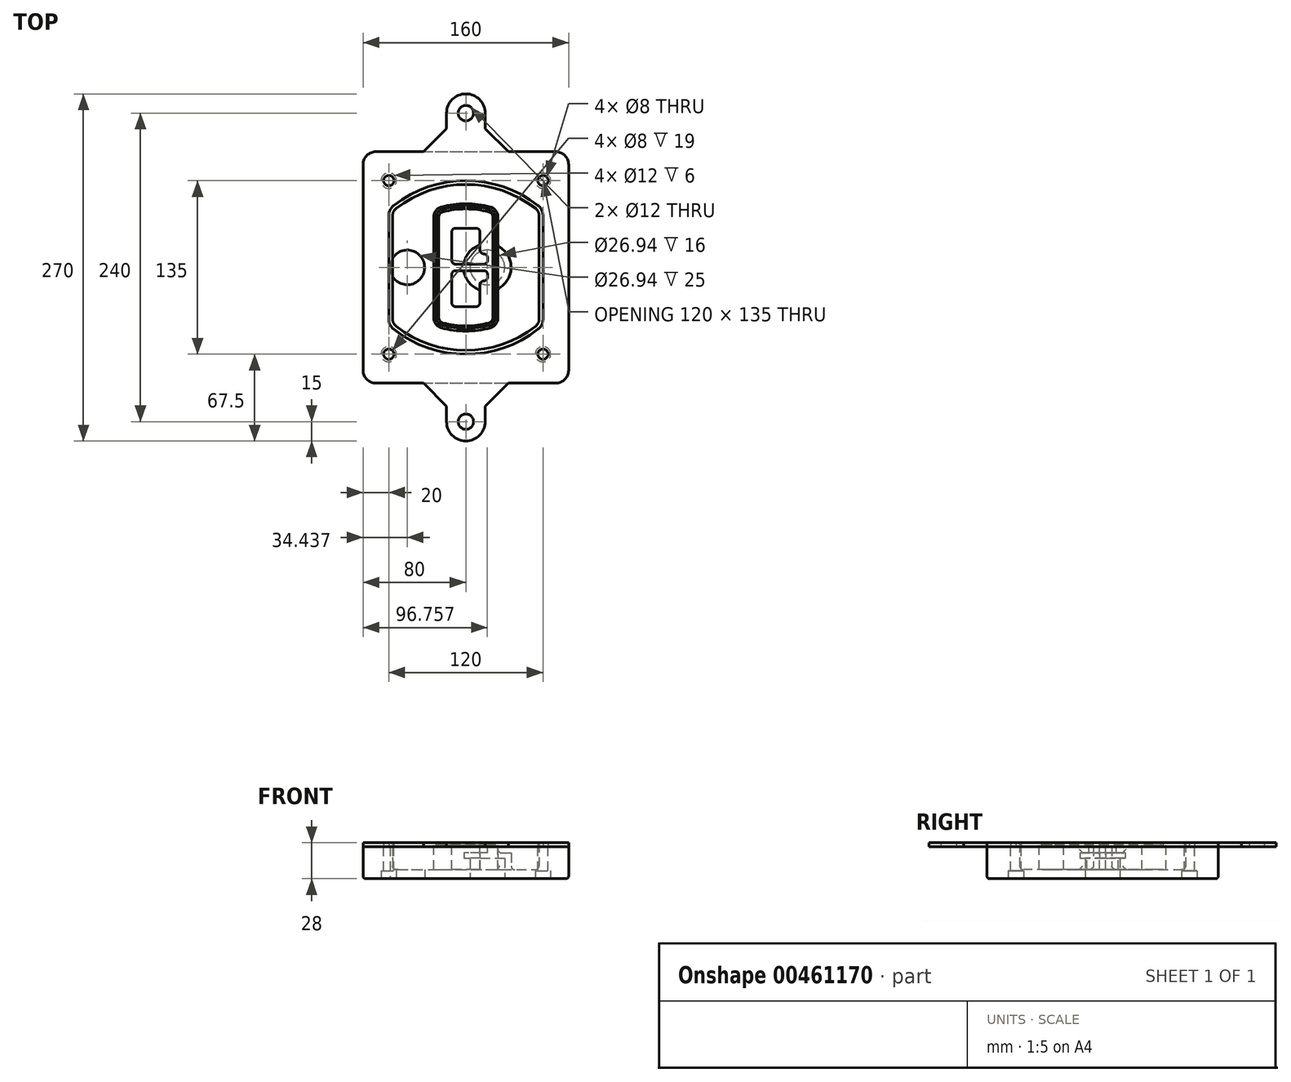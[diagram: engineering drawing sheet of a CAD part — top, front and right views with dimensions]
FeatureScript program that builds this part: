
annotation { "Feature Type Name" : "Feature", "Feature Type Description" : "" }
export const myFeature = defineFeature(function(context is Context, id is Id, definition is map)
    precondition{}
    {
        {
            var Q0;
            Q0=qCreatedBy(makeId("Top.planeOp"),FACE);
            var sketch = newSketch(context, id + "F0", { "sketchPlane" : qUnion([Q0])});
            skPoint(sketch, "E0.rect.middle", {"position": v(0, 0) * mm});
            skLineSegment(sketch, "E1.bottom", {"start": v(-70, -90) * mm, "end": v(70, -90) * mm});
            skLineSegment(sketch, "E1.top", {"start": v(-70, 90) * mm, "end": v(70, 90) * mm});
            skLineSegment(sketch, "E1.left", {"start": v(-80, -80) * mm, "end": v(-80, 80) * mm});
            skLineSegment(sketch, "E1.right", {"start": v(80, -80) * mm, "end": v(80, 80) * mm});
            skLineSegment(sketch, "E2", {"start": v(-80, 90) * mm, "end": v(80, -90) * mm, "construction": true});
            skLineSegment(sketch, "E3", {"start": v(80, 90) * mm, "end": v(-80, -90) * mm, "construction": true});
            skCircle(sketch, "E4", {"center": v(-60, 67.5) * mm, "radius": 4 * mm});
            skCircle(sketch, "E5", {"center": v(60, 67.5) * mm, "radius": 4 * mm});
            skCircle(sketch, "E6", {"center": v(60, -67.5) * mm, "radius": 4 * mm});
            skCircle(sketch, "E7", {"center": v(-60, -67.5) * mm, "radius": 4 * mm});
            skLineSegment(sketch, "E8", {"start": v(-60, 67.5) * mm, "end": v(60, 67.5) * mm, "construction": true});
            skLineSegment(sketch, "E9", {"start": v(60, 67.5) * mm, "end": v(60, -67.5) * mm, "construction": true});
            skLineSegment(sketch, "E10", {"start": v(60, -67.5) * mm, "end": v(-60, -67.5) * mm, "construction": true});
            skLineSegment(sketch, "E11", {"start": v(-60, -67.5) * mm, "end": v(-60, 67.5) * mm, "construction": true});
            skLineSegment(sketch, "E12", {"start": v(-60, 40.3) * mm, "end": v(-60, -40.3) * mm});
            skLineSegment(sketch, "E13", {"start": v(60, 40.3) * mm, "end": v(60, -40.3) * mm});
            skArc(sketch, "E14", {"start": v(56.15, 48.18) * mm, "mid": v(0, 67.5) * mm, "end": v(-56.15, 48.18) * mm});
            skArc(sketch, "E15", {"start": v(-56.15, -48.18) * mm, "mid": v(0, -67.5) * mm, "end": v(56.15, -48.18) * mm});
            skLineSegment(sketch, "E16", {"start": v(-60, 0) * mm, "end": v(60, 0) * mm, "construction": true});
            skPoint(sketch, "E17.visualSharp", {"position": v(-60, -45) * mm});
            skArc(sketch, "E17.filletArc", {"start": v(-60, -40.3) * mm, "mid": v(-58.99, -44.68) * mm, "end": v(-56.15, -48.18) * mm});
            skPoint(sketch, "E18.visualSharp", {"position": v(-60, 45) * mm});
            skArc(sketch, "E18.filletArc", {"start": v(-56.15, 48.18) * mm, "mid": v(-58.99, 44.68) * mm, "end": v(-60, 40.3) * mm});
            skPoint(sketch, "E19.visualSharp", {"position": v(60, 45) * mm});
            skArc(sketch, "E19.filletArc", {"start": v(60, 40.3) * mm, "mid": v(58.99, 44.68) * mm, "end": v(56.15, 48.18) * mm});
            skPoint(sketch, "E20.visualSharp", {"position": v(60, -45) * mm});
            skArc(sketch, "E20.filletArc", {"start": v(56.15, -48.18) * mm, "mid": v(58.99, -44.68) * mm, "end": v(60, -40.3) * mm});
            skPoint(sketch, "E21.visualSharp", {"position": v(-80, 90) * mm});
            skArc(sketch, "E21.filletArc", {"start": v(-70, 90) * mm, "mid": v(-77.07, 87.07) * mm, "end": v(-80, 80) * mm});
            skPoint(sketch, "E22.visualSharp", {"position": v(80, 90) * mm});
            skArc(sketch, "E22.filletArc", {"start": v(80, 80) * mm, "mid": v(77.07, 87.07) * mm, "end": v(70, 90) * mm});
            skPoint(sketch, "E23.visualSharp", {"position": v(80, -90) * mm});
            skArc(sketch, "E23.filletArc", {"start": v(70, -90) * mm, "mid": v(77.07, -87.07) * mm, "end": v(80, -80) * mm});
            skPoint(sketch, "E24.visualSharp", {"position": v(-80, -90) * mm});
            skArc(sketch, "E24.filletArc", {"start": v(-80, -80) * mm, "mid": v(-77.07, -87.07) * mm, "end": v(-70, -90) * mm});
            skArc(sketch, "E25.0", {"start": v(57, 40.3) * mm, "mid": v(56.3, 43.36) * mm, "end": v(54.3, 45.81) * mm});
            skLineSegment(sketch, "E25.1", {"start": v(57, 40.3) * mm, "end": v(57, -40.3) * mm});
            skArc(sketch, "E25.2", {"start": v(54.3, -45.81) * mm, "mid": v(56.3, -43.36) * mm, "end": v(57, -40.3) * mm});
            skArc(sketch, "E25.3", {"start": v(-54.3, -45.81) * mm, "mid": v(0, -64.5) * mm, "end": v(54.3, -45.81) * mm});
            skArc(sketch, "E25.4", {"start": v(-57, -40.3) * mm, "mid": v(-56.3, -43.36) * mm, "end": v(-54.3, -45.81) * mm});
            skArc(sketch, "E25.5", {"start": v(54.3, 45.81) * mm, "mid": v(0, 64.5) * mm, "end": v(-54.3, 45.81) * mm});
            skLineSegment(sketch, "E25.6", {"start": v(-57, 40.3) * mm, "end": v(-57, -40.3) * mm});
            skArc(sketch, "E25.7", {"start": v(-54.3, 45.81) * mm, "mid": v(-56.3, 43.36) * mm, "end": v(-57, 40.3) * mm});
            skArc(sketch, "E26.0", {"start": v(-58.62, 51.33) * mm, "mid": v(-62.58, 46.43) * mm, "end": v(-64, 40.3) * mm});
            skArc(sketch, "E26.1", {"start": v(58.62, 51.33) * mm, "mid": v(0, 71.5) * mm, "end": v(-58.62, 51.33) * mm});
            skArc(sketch, "E26.2", {"start": v(64, 40.3) * mm, "mid": v(62.58, 46.43) * mm, "end": v(58.62, 51.33) * mm});
            skLineSegment(sketch, "E26.3", {"start": v(64, 40.3) * mm, "end": v(64, -40.3) * mm});
            skArc(sketch, "E26.4", {"start": v(58.62, -51.33) * mm, "mid": v(62.58, -46.43) * mm, "end": v(64, -40.3) * mm});
            skLineSegment(sketch, "E26.5", {"start": v(-64, 40.3) * mm, "end": v(-64, -40.3) * mm});
            skArc(sketch, "E26.6", {"start": v(-58.62, -51.33) * mm, "mid": v(0, -71.5) * mm, "end": v(58.62, -51.33) * mm});
            skArc(sketch, "E26.7", {"start": v(-64, -40.3) * mm, "mid": v(-62.58, -46.43) * mm, "end": v(-58.62, -51.33) * mm});
            skSolve(sketch);
        }
        {
            var Q0;
            Q0=makeQuery(id+"F0.imprint","IMPRINT",FACE,{"disambiguationData":[TD([[makeQuery(id+"F0.imprint","IMPRINT",EDGE,{"derivedFrom":sQuery(id+"F0.wireOp",EDGE,"E1.bottom")}),1.0]])]});
            var Q1;
            Q1=makeQuery(id+"F0.imprint","IMPRINT",FACE,{"disambiguationData":[TD([[makeQuery(id+"F0.imprint","IMPRINT",EDGE,{"derivedFrom":sQuery(id+"F0.wireOp",EDGE,"E12")}),1.0]])]});
            var Q2;
            Q2=makeQuery(id+"F0.imprint","IMPRINT",FACE,{"disambiguationData":[TD([[makeQuery(id+"F0.imprint","IMPRINT",EDGE,{"derivedFrom":sQuery(id+"F0.wireOp",EDGE,"E25.0")}),1.0]])]});
            var Q3;
            Q3=makeQuery(id+"F0.imprint","IMPRINT",FACE,{"disambiguationData":[TD([[makeQuery(id+"F0.imprint","IMPRINT",EDGE,{"derivedFrom":sQuery(id+"F0.wireOp",EDGE,"E12")}),-1.0]])]});
            extrude(context, id + "F1", {"entities" : qUnion([Q0, Q1, Q2, Q3]), "oppositeDirection" : true, "depth" : 25 * mm});
        }
        {
            var Q0;
            Q0=makeQuery(id+"F0.imprint","IMPRINT",FACE,{"disambiguationData":[TD([[makeQuery(id+"F0.imprint","IMPRINT",EDGE,{"derivedFrom":sQuery(id+"F0.wireOp",EDGE,"E12")}),1.0]])]});
            extrude(context, id + "F2", {"entities" : qUnion([Q0]), "operationType" : NewBodyOperationType.ADD, "depth" : 3 * mm});
        }
        {
            var Q0;
            Q0=makeQuery(id+"F0.imprint","IMPRINT",FACE,{"disambiguationData":[TD([[makeQuery(id+"F0.imprint","IMPRINT",EDGE,{"derivedFrom":sQuery(id+"F0.wireOp",EDGE,"E25.0")}),1.0]])]});
            extrude(context, id + "F3", {"entities" : qUnion([Q0]), "operationType" : NewBodyOperationType.REMOVE, "oppositeDirection" : true, "depth" : 18 * mm});
        }
        {
            var Q0;
            Q0=makeQuery(id+"F2.opExtrude","CAP_FACE",FACE,{"disambiguationData":[OSD([sQuery(id+"F0.wireOp",EDGE,"E12"),sQuery(id+"F0.wireOp",EDGE,"E13"),sQuery(id+"F0.wireOp",EDGE,"E14"),sQuery(id+"F0.wireOp",EDGE,"E15"),sQuery(id+"F0.wireOp",EDGE,"E17.filletArc"),sQuery(id+"F0.wireOp",EDGE,"E18.filletArc"),sQuery(id+"F0.wireOp",EDGE,"E19.filletArc"),sQuery(id+"F0.wireOp",EDGE,"E20.filletArc"),sQuery(id+"F0.wireOp",EDGE,"E25.0"),sQuery(id+"F0.wireOp",EDGE,"E25.1"),sQuery(id+"F0.wireOp",EDGE,"E25.2"),sQuery(id+"F0.wireOp",EDGE,"E25.3"),sQuery(id+"F0.wireOp",EDGE,"E25.4"),sQuery(id+"F0.wireOp",EDGE,"E25.5"),sQuery(id+"F0.wireOp",EDGE,"E25.6"),sQuery(id+"F0.wireOp",EDGE,"E25.7")])],"isStart":false});
            var sketch = newSketch(context, id + "F4", { "sketchPlane" : qUnion([Q0])});
            skArc(sketch, "E27.0", {"start": v(-19.08, -46.97) * mm, "mid": v(0, -49.5) * mm, "end": v(19.08, -46.97) * mm});
            skArc(sketch, "E28.0", {"start": v(19.08, 46.97) * mm, "mid": v(0, 49.5) * mm, "end": v(-19.08, 46.97) * mm});
            skLineSegment(sketch, "E29", {"start": v(-25, 39.25) * mm, "end": v(-25, -39.25) * mm});
            skLineSegment(sketch, "E30", {"start": v(25, 39.25) * mm, "end": v(25, -39.25) * mm});
            skLineSegment(sketch, "E31", {"start": v(-25, 45.1) * mm, "end": v(25, 45.1) * mm, "construction": true});
            skLineSegment(sketch, "E32", {"start": v(-25, -45.1) * mm, "end": v(25, -45.1) * mm, "construction": true});
            skPoint(sketch, "E33.visualSharp", {"position": v(-25, 45.1) * mm});
            skArc(sketch, "E33.filletArc", {"start": v(-19.08, 46.97) * mm, "mid": v(-23.35, 44.11) * mm, "end": v(-25, 39.25) * mm});
            skPoint(sketch, "E34.visualSharp", {"position": v(25, 45.1) * mm});
            skArc(sketch, "E34.filletArc", {"start": v(25, 39.25) * mm, "mid": v(23.35, 44.11) * mm, "end": v(19.08, 46.97) * mm});
            skPoint(sketch, "E35.visualSharp", {"position": v(25, -45.1) * mm});
            skArc(sketch, "E35.filletArc", {"start": v(19.08, -46.97) * mm, "mid": v(23.35, -44.11) * mm, "end": v(25, -39.25) * mm});
            skPoint(sketch, "E36.visualSharp", {"position": v(-25, -45.1) * mm});
            skArc(sketch, "E36.filletArc", {"start": v(-25, -39.25) * mm, "mid": v(-23.35, -44.11) * mm, "end": v(-19.08, -46.97) * mm});
            skArc(sketch, "E37.0", {"start": v(54.3, 45.81) * mm, "mid": v(0, 64.5) * mm, "end": v(-54.3, 45.81) * mm});
            skArc(sketch, "E37.1", {"start": v(-54.3, 45.81) * mm, "mid": v(-56.3, 43.36) * mm, "end": v(-57, 40.3) * mm});
            skLineSegment(sketch, "E37.2", {"start": v(-57, 40.3) * mm, "end": v(-57, -40.3) * mm});
            skArc(sketch, "E37.3", {"start": v(-57, -40.3) * mm, "mid": v(-56.3, -43.36) * mm, "end": v(-54.3, -45.81) * mm});
            skArc(sketch, "E37.4", {"start": v(-54.3, -45.81) * mm, "mid": v(0, -64.5) * mm, "end": v(54.3, -45.81) * mm});
            skArc(sketch, "E37.5", {"start": v(54.3, -45.81) * mm, "mid": v(56.3, -43.36) * mm, "end": v(57, -40.3) * mm});
            skLineSegment(sketch, "E37.6", {"start": v(57, 40.3) * mm, "end": v(57, -40.3) * mm});
            skArc(sketch, "E37.7", {"start": v(57, 40.3) * mm, "mid": v(56.3, 43.36) * mm, "end": v(54.3, 45.81) * mm});
            skLineSegment(sketch, "E38.0", {"start": v(23, 39.25) * mm, "end": v(23, -39.25) * mm});
            skArc(sketch, "E38.1", {"start": v(18.56, -45.04) * mm, "mid": v(21.76, -42.9) * mm, "end": v(23, -39.25) * mm});
            skArc(sketch, "E38.2", {"start": v(-18.56, -45.04) * mm, "mid": v(0, -47.5) * mm, "end": v(18.56, -45.04) * mm});
            skArc(sketch, "E38.3", {"start": v(-23, -39.25) * mm, "mid": v(-21.76, -42.9) * mm, "end": v(-18.56, -45.04) * mm});
            skLineSegment(sketch, "E38.4", {"start": v(-23, 39.25) * mm, "end": v(-23, -39.25) * mm});
            skArc(sketch, "E38.5", {"start": v(23, 39.25) * mm, "mid": v(21.76, 42.9) * mm, "end": v(18.56, 45.04) * mm});
            skArc(sketch, "E38.6", {"start": v(-18.56, 45.04) * mm, "mid": v(-21.76, 42.9) * mm, "end": v(-23, 39.25) * mm});
            skArc(sketch, "E38.7", {"start": v(18.56, 45.04) * mm, "mid": v(0, 47.5) * mm, "end": v(-18.56, 45.04) * mm});
            skArc(sketch, "E39.0", {"start": v(21, 39.25) * mm, "mid": v(20.18, 41.68) * mm, "end": v(18.04, 43.1) * mm});
            skLineSegment(sketch, "E39.1", {"start": v(21, 39.25) * mm, "end": v(21, -39.25) * mm});
            skArc(sketch, "E39.2", {"start": v(18.04, -43.1) * mm, "mid": v(20.18, -41.68) * mm, "end": v(21, -39.25) * mm});
            skArc(sketch, "E39.3", {"start": v(-18.04, -43.1) * mm, "mid": v(0, -45.5) * mm, "end": v(18.04, -43.1) * mm});
            skArc(sketch, "E39.4", {"start": v(-21, -39.25) * mm, "mid": v(-20.18, -41.68) * mm, "end": v(-18.04, -43.1) * mm});
            skArc(sketch, "E39.5", {"start": v(18.04, 43.1) * mm, "mid": v(0, 45.5) * mm, "end": v(-18.04, 43.1) * mm});
            skLineSegment(sketch, "E39.6", {"start": v(-21, 39.25) * mm, "end": v(-21, -39.25) * mm});
            skArc(sketch, "E39.7", {"start": v(-18.04, 43.1) * mm, "mid": v(-20.18, 41.68) * mm, "end": v(-21, 39.25) * mm});
            skLineSegment(sketch, "E40", {"start": v(-25, 0) * mm, "end": v(25, 0) * mm, "construction": true});
            skLineSegment(sketch, "E41", {"start": v(-11, 5.5) * mm, "end": v(-11, 27.5) * mm});
            skLineSegment(sketch, "E42", {"start": v(-8, 30.5) * mm, "end": v(8, 30.5) * mm});
            skLineSegment(sketch, "E43", {"start": v(11, 27.5) * mm, "end": v(11, 13.5) * mm});
            skLineSegment(sketch, "E44", {"start": v(14, 10.5) * mm, "end": v(14, 10.5) * mm});
            skLineSegment(sketch, "E45", {"start": v(17, 7.5) * mm, "end": v(17, 5.5) * mm});
            skLineSegment(sketch, "E46", {"start": v(14, 2.5) * mm, "end": v(-8, 2.5) * mm});
            skPoint(sketch, "E47.visualSharp", {"position": v(-11, 30.5) * mm});
            skArc(sketch, "E47.filletArc", {"start": v(-8, 30.5) * mm, "mid": v(-10.12, 29.62) * mm, "end": v(-11, 27.5) * mm});
            skPoint(sketch, "E48.visualSharp", {"position": v(11, 30.5) * mm});
            skArc(sketch, "E48.filletArc", {"start": v(11, 27.5) * mm, "mid": v(10.12, 29.62) * mm, "end": v(8, 30.5) * mm});
            skPoint(sketch, "E49.visualSharp", {"position": v(11, 10.5) * mm});
            skArc(sketch, "E49.filletArc", {"start": v(11, 13.5) * mm, "mid": v(11.88, 11.38) * mm, "end": v(14, 10.5) * mm});
            skPoint(sketch, "E50.visualSharp", {"position": v(17, 10.5) * mm});
            skArc(sketch, "E50.filletArc", {"start": v(17, 7.5) * mm, "mid": v(16.12, 9.62) * mm, "end": v(14, 10.5) * mm});
            skPoint(sketch, "E51.visualSharp", {"position": v(17, 2.5) * mm});
            skArc(sketch, "E51.filletArc", {"start": v(14, 2.5) * mm, "mid": v(16.12, 3.38) * mm, "end": v(17, 5.5) * mm});
            skPoint(sketch, "E52.visualSharp", {"position": v(-11, 2.5) * mm});
            skArc(sketch, "E52.filletArc", {"start": v(-11, 5.5) * mm, "mid": v(-10.12, 3.38) * mm, "end": v(-8, 2.5) * mm});
            skLineSegment(sketch, "E53.0.MirrorCS", {"start": v(14, -2.5) * mm, "end": v(-8, -2.5) * mm});
            skArc(sketch, "E54.0.MirrorCS", {"start": v(-11, -5.5) * mm, "mid": v(-10.12, -3.38) * mm, "end": v(-8, -2.5) * mm});
            skLineSegment(sketch, "E55.0.MirrorCS", {"start": v(-11, -5.5) * mm, "end": v(-11, -27.5) * mm});
            skArc(sketch, "E56.0.MirrorCS", {"start": v(-8, -30.5) * mm, "mid": v(-10.12, -29.62) * mm, "end": v(-11, -27.5) * mm});
            skLineSegment(sketch, "E57.0.MirrorCS", {"start": v(-8, -30.5) * mm, "end": v(8, -30.5) * mm});
            skArc(sketch, "E58.0.MirrorCS", {"start": v(11, -27.5) * mm, "mid": v(10.12, -29.62) * mm, "end": v(8, -30.5) * mm});
            skLineSegment(sketch, "E59.0.MirrorCS", {"start": v(11, -27.5) * mm, "end": v(11, -13.5) * mm});
            skArc(sketch, "E60.0.MirrorCS", {"start": v(11, -13.5) * mm, "mid": v(11.88, -11.38) * mm, "end": v(14, -10.5) * mm});
            skArc(sketch, "E61.0.MirrorCS", {"start": v(17, -7.5) * mm, "mid": v(16.12, -9.62) * mm, "end": v(14, -10.5) * mm});
            skLineSegment(sketch, "E62.0.MirrorCS", {"start": v(17, -7.5) * mm, "end": v(17, -5.5) * mm});
            skArc(sketch, "E63.0.MirrorCS", {"start": v(14, -2.5) * mm, "mid": v(16.12, -3.38) * mm, "end": v(17, -5.5) * mm});
            skSolve(sketch);
        }
        {
            var Q0;
            Q0=makeQuery(id+"F4.imprint","IMPRINT",FACE,{"disambiguationData":[TD([[makeQuery(id+"F4.imprint","IMPRINT",EDGE,{"derivedFrom":sQuery(id+"F4.wireOp",EDGE,"E27.0")}),1.0]])]});
            var Q1;
            Q1=makeQuery(id+"F4.imprint","IMPRINT",FACE,{"disambiguationData":[TD([[makeQuery(id+"F4.imprint","IMPRINT",EDGE,{"derivedFrom":sQuery(id+"F4.wireOp",EDGE,"E38.0")}),-1.0]])]});
            var Q2;
            Q2=makeQuery(id+"F4.imprint","IMPRINT",FACE,{"disambiguationData":[TD([[makeQuery(id+"F4.imprint","IMPRINT",EDGE,{"derivedFrom":sQuery(id+"F4.wireOp",EDGE,"E39.0")}),1.0]])]});
            extrude(context, id + "F5", {"entities" : qUnion([Q0, Q1, Q2]), "operationType" : NewBodyOperationType.ADD, "endBound" : BoundingType.UP_TO_NEXT, "oppositeDirection" : true, "depth" : 25 * mm});
        }
        {
            var Q0;
            Q0=makeQuery(id+"F4.imprint","IMPRINT",FACE,{"disambiguationData":[TD([[makeQuery(id+"F4.imprint","IMPRINT",EDGE,{"derivedFrom":sQuery(id+"F4.wireOp",EDGE,"E38.0")}),-1.0]])]});
            extrude(context, id + "F6", {"entities" : qUnion([Q0]), "operationType" : NewBodyOperationType.REMOVE, "oppositeDirection" : true, "depth" : 2 * mm});
        }
        {
            var Q0;
            Q0=makeQuery(id+"F1.opExtrude","CAP_FACE",FACE,{"disambiguationData":[OSD([sQuery(id+"F0.wireOp",EDGE,"E1.bottom"),sQuery(id+"F0.wireOp",EDGE,"E1.top"),sQuery(id+"F0.wireOp",EDGE,"E1.left"),sQuery(id+"F0.wireOp",EDGE,"E1.right"),sQuery(id+"F0.wireOp",EDGE,"E4"),sQuery(id+"F0.wireOp",EDGE,"E5"),sQuery(id+"F0.wireOp",EDGE,"E6"),sQuery(id+"F0.wireOp",EDGE,"E7"),sQuery(id+"F0.wireOp",EDGE,"E21.filletArc"),sQuery(id+"F0.wireOp",EDGE,"E22.filletArc"),sQuery(id+"F0.wireOp",EDGE,"E23.filletArc"),sQuery(id+"F0.wireOp",EDGE,"E24.filletArc")])],"isStart":false});
            var sketch = newSketch(context, id + "F7", { "sketchPlane" : qUnion([Q0])});
            skCircle(sketch, "E64", {"center": v(16.76, 0) * mm, "radius": 13.47 * mm});
            skCircle(sketch, "E65", {"center": v(-45.56, 0) * mm, "radius": 13.47 * mm});
            skLineSegment(sketch, "E66", {"start": v(80, 0) * mm, "end": v(-80, 0) * mm});
            skCircle(sketch, "E67", {"center": v(16.76, 0) * mm, "radius": 18.47 * mm});
            skCircle(sketch, "E68", {"center": v(60, -67.5) * mm, "radius": 6 * mm});
            skCircle(sketch, "E69", {"center": v(-60, -67.5) * mm, "radius": 6 * mm});
            skCircle(sketch, "E70", {"center": v(-60, 67.5) * mm, "radius": 6 * mm});
            skCircle(sketch, "E71", {"center": v(60, 67.5) * mm, "radius": 6 * mm});
            skSolve(sketch);
        }
        {
            var Q0;
            {var subQ1=sQuery(id+"F7.wireOp",EDGE,"E66");var subQ4=sQuery(id+"F7.wireOp",EDGE,"E64");var subQ6=makeQuery(id+"F7.imprint","INTERSECT",VERTEX,{"disambiguationData":[OD(0.0)],"derivedFrom":[subQ4,subQ1]});Q0=makeQuery(id+"F7.imprint","IMPRINT",FACE,{"disambiguationData":[TD([[makeQuery(id+"F7.imprint","IMPRINT",EDGE,{"disambiguationData":[TD([[subQ6,-1.0]])],"derivedFrom":subQ4}),-1.0]])]});}
            var Q1;
            {var subQ0=sQuery(id+"F7.wireOp",EDGE,"E66");var subQ1=sQuery(id+"F7.wireOp",EDGE,"E64");var subQ3=makeQuery(id+"F7.imprint","INTERSECT",VERTEX,{"disambiguationData":[OD(0.0)],"derivedFrom":[subQ1,subQ0]});Q1=makeQuery(id+"F7.imprint","IMPRINT",FACE,{"disambiguationData":[TD([[makeQuery(id+"F7.imprint","IMPRINT",EDGE,{"disambiguationData":[TD([[subQ3,-1.0]])],"derivedFrom":subQ1}),1.0]])]});}
            var Q2;
            {var subQ0=sQuery(id+"F7.wireOp",EDGE,"E66");var subQ1=sQuery(id+"F7.wireOp",EDGE,"E64");var subQ3=makeQuery(id+"F7.imprint","INTERSECT",VERTEX,{"disambiguationData":[OD(0.0)],"derivedFrom":[subQ1,subQ0]});Q2=makeQuery(id+"F7.imprint","IMPRINT",FACE,{"disambiguationData":[TD([[makeQuery(id+"F7.imprint","IMPRINT",EDGE,{"disambiguationData":[TD([[subQ3,1.0]])],"derivedFrom":subQ1}),1.0]])]});}
            var Q3;
            {var subQ1=sQuery(id+"F7.wireOp",EDGE,"E66");var subQ4=sQuery(id+"F7.wireOp",EDGE,"E64");var subQ6=makeQuery(id+"F7.imprint","INTERSECT",VERTEX,{"disambiguationData":[OD(0.0)],"derivedFrom":[subQ4,subQ1]});Q3=makeQuery(id+"F7.imprint","IMPRINT",FACE,{"disambiguationData":[TD([[makeQuery(id+"F7.imprint","IMPRINT",EDGE,{"disambiguationData":[TD([[subQ6,1.0]])],"derivedFrom":subQ4}),-1.0]])]});}
            extrude(context, id + "F8", {"entities" : qUnion([Q0, Q1, Q2, Q3]), "operationType" : NewBodyOperationType.ADD, "oppositeDirection" : true, "depth" : 20 * mm});
        }
        {
            var Q0;
            {var subQ0=sQuery(id+"F7.wireOp",EDGE,"E66");var subQ1=sQuery(id+"F7.wireOp",EDGE,"E64");var subQ3=makeQuery(id+"F7.imprint","INTERSECT",VERTEX,{"disambiguationData":[OD(0.0)],"derivedFrom":[subQ1,subQ0]});Q0=makeQuery(id+"F7.imprint","IMPRINT",FACE,{"disambiguationData":[TD([[makeQuery(id+"F7.imprint","IMPRINT",EDGE,{"disambiguationData":[TD([[subQ3,-1.0]])],"derivedFrom":subQ1}),1.0]])]});}
            var Q1;
            {var subQ0=sQuery(id+"F7.wireOp",EDGE,"E66");var subQ1=sQuery(id+"F7.wireOp",EDGE,"E64");var subQ3=makeQuery(id+"F7.imprint","INTERSECT",VERTEX,{"disambiguationData":[OD(0.0)],"derivedFrom":[subQ1,subQ0]});Q1=makeQuery(id+"F7.imprint","IMPRINT",FACE,{"disambiguationData":[TD([[makeQuery(id+"F7.imprint","IMPRINT",EDGE,{"disambiguationData":[TD([[subQ3,1.0]])],"derivedFrom":subQ1}),1.0]])]});}
            extrude(context, id + "F9", {"entities" : qUnion([Q0, Q1]), "operationType" : NewBodyOperationType.REMOVE, "oppositeDirection" : true, "depth" : 16 * mm});
        }
        {
            var Q0;
            {var subQ0=sQuery(id+"F7.wireOp",EDGE,"E66");var subQ1=sQuery(id+"F7.wireOp",EDGE,"E65");var subQ3=makeQuery(id+"F7.imprint","INTERSECT",VERTEX,{"disambiguationData":[OD(0.0)],"derivedFrom":[subQ1,subQ0]});Q0=makeQuery(id+"F7.imprint","IMPRINT",FACE,{"disambiguationData":[TD([[makeQuery(id+"F7.imprint","IMPRINT",EDGE,{"disambiguationData":[TD([[subQ3,-1.0]])],"derivedFrom":subQ1}),1.0]])]});}
            var Q1;
            {var subQ0=sQuery(id+"F7.wireOp",EDGE,"E66");var subQ1=sQuery(id+"F7.wireOp",EDGE,"E65");var subQ3=makeQuery(id+"F7.imprint","INTERSECT",VERTEX,{"disambiguationData":[OD(0.0)],"derivedFrom":[subQ1,subQ0]});Q1=makeQuery(id+"F7.imprint","IMPRINT",FACE,{"disambiguationData":[TD([[makeQuery(id+"F7.imprint","IMPRINT",EDGE,{"disambiguationData":[TD([[subQ3,1.0]])],"derivedFrom":subQ1}),1.0]])]});}
            extrude(context, id + "F10", {"entities" : qUnion([Q0, Q1]), "operationType" : NewBodyOperationType.REMOVE, "oppositeDirection" : true, "depth" : 25 * mm});
        }
        {
            var Q0;
            Q0=makeQuery(id+"F7.imprint","IMPRINT",FACE,{"disambiguationData":[TD([[makeQuery(id+"F7.imprint","IMPRINT",EDGE,{"derivedFrom":sQuery(id+"F7.wireOp",EDGE,"E68")}),1.0]])]});
            var Q1;
            Q1=makeQuery(id+"F7.imprint","IMPRINT",FACE,{"disambiguationData":[TD([[makeQuery(id+"F7.imprint","IMPRINT",EDGE,{"derivedFrom":makeQuery(id+"F1.opExtrude","CAP_EDGE",EDGE,{"disambiguationData":[OSD([sQuery(id+"F0.wireOp",EDGE,"E5")])],"isStart":false})}),-1.0]])]});
            var Q2;
            Q2=makeQuery(id+"F7.imprint","IMPRINT",FACE,{"disambiguationData":[TD([[makeQuery(id+"F7.imprint","IMPRINT",EDGE,{"derivedFrom":sQuery(id+"F7.wireOp",EDGE,"E69")}),1.0]])]});
            var Q3;
            Q3=makeQuery(id+"F7.imprint","IMPRINT",FACE,{"disambiguationData":[TD([[makeQuery(id+"F7.imprint","IMPRINT",EDGE,{"derivedFrom":makeQuery(id+"F1.opExtrude","CAP_EDGE",EDGE,{"disambiguationData":[OSD([sQuery(id+"F0.wireOp",EDGE,"E4")])],"isStart":false})}),-1.0]])]});
            var Q4;
            Q4=makeQuery(id+"F7.imprint","IMPRINT",FACE,{"disambiguationData":[TD([[makeQuery(id+"F7.imprint","IMPRINT",EDGE,{"derivedFrom":sQuery(id+"F7.wireOp",EDGE,"E70")}),1.0]])]});
            var Q5;
            Q5=makeQuery(id+"F7.imprint","IMPRINT",FACE,{"disambiguationData":[TD([[makeQuery(id+"F7.imprint","IMPRINT",EDGE,{"derivedFrom":makeQuery(id+"F1.opExtrude","CAP_EDGE",EDGE,{"disambiguationData":[OSD([sQuery(id+"F0.wireOp",EDGE,"E7")])],"isStart":false})}),-1.0]])]});
            var Q6;
            Q6=makeQuery(id+"F7.imprint","IMPRINT",FACE,{"disambiguationData":[TD([[makeQuery(id+"F7.imprint","IMPRINT",EDGE,{"derivedFrom":sQuery(id+"F7.wireOp",EDGE,"E71")}),1.0]])]});
            var Q7;
            Q7=makeQuery(id+"F7.imprint","IMPRINT",FACE,{"disambiguationData":[TD([[makeQuery(id+"F7.imprint","IMPRINT",EDGE,{"derivedFrom":makeQuery(id+"F1.opExtrude","CAP_EDGE",EDGE,{"disambiguationData":[OSD([sQuery(id+"F0.wireOp",EDGE,"E6")])],"isStart":false})}),-1.0]])]});
            extrude(context, id + "F11", {"entities" : qUnion([Q0, Q1, Q2, Q3, Q4, Q5, Q6, Q7]), "operationType" : NewBodyOperationType.REMOVE, "oppositeDirection" : true, "depth" : 6 * mm});
        }
        {
            var Q0;
            Q0=makeQuery(id+"F9.boolean.opBoolean","COPY",FACE,{"derivedFrom":makeQuery(id+"F9.opExtrude","CAP_FACE",FACE,{"disambiguationData":[OSD([sQuery(id+"F7.wireOp",EDGE,"E64")])],"isStart":false})});
            var sketch = newSketch(context, id + "F12", { "sketchPlane" : qUnion([Q0])});
            skArc(sketch, "E72.0", {"start": v(11, 17.55) * mm, "mid": v(2.57, 11.82) * mm, "end": v(-1.54, 2.5) * mm});
            skArc(sketch, "E72.1", {"start": v(-1.54, -2.5) * mm, "mid": v(2.57, -11.82) * mm, "end": v(11, -17.55) * mm});
            skLineSegment(sketch, "E73", {"start": v(-1.54, -2.5) * mm, "end": v(14, -2.5) * mm});
            skLineSegment(sketch, "E74.0", {"start": v(14, 2.5) * mm, "end": v(-1.54, 2.5) * mm});
            skArc(sketch, "E74.1", {"start": v(14, 2.5) * mm, "mid": v(16.12, 3.38) * mm, "end": v(17, 5.5) * mm});
            skLineSegment(sketch, "E74.2", {"start": v(17, 7.5) * mm, "end": v(17, 5.5) * mm});
            skArc(sketch, "E74.3", {"start": v(17, 7.5) * mm, "mid": v(16.12, 9.62) * mm, "end": v(14, 10.5) * mm});
            skArc(sketch, "E74.4", {"start": v(11, 13.5) * mm, "mid": v(11.88, 11.38) * mm, "end": v(14, 10.5) * mm});
            skLineSegment(sketch, "E74.5", {"start": v(11, 17.55) * mm, "end": v(11, 13.5) * mm});
            skLineSegment(sketch, "E74.7", {"start": v(14, -2.5) * mm, "end": v(-1.54, -2.5) * mm});
            skArc(sketch, "E74.8", {"start": v(14, -2.5) * mm, "mid": v(16.12, -3.38) * mm, "end": v(17, -5.5) * mm});
            skLineSegment(sketch, "E74.9", {"start": v(17, -7.5) * mm, "end": v(17, -5.5) * mm});
            skArc(sketch, "E74.10", {"start": v(17, -7.5) * mm, "mid": v(16.12, -9.62) * mm, "end": v(14, -10.5) * mm});
            skArc(sketch, "E74.11", {"start": v(11, -13.5) * mm, "mid": v(11.88, -11.38) * mm, "end": v(14, -10.5) * mm});
            skLineSegment(sketch, "E74.12", {"start": v(11, -17.55) * mm, "end": v(11, -13.5) * mm});
            skPoint(sketch, "E75.orphan", {"position": v(11, -27.5) * mm});
            skPoint(sketch, "E76.orphan", {"position": v(-8, -2.5) * mm});
            skPoint(sketch, "E77.orphan", {"position": v(-8, 2.5) * mm});
            skPoint(sketch, "E78.orphan", {"position": v(11, 27.5) * mm});
            skSolve(sketch);
        }
        {
            var Q0;
            {var subQ7=sQuery(id+"F12.wireOp",EDGE,"E72.0");var subQ14=sQuery(id+"F12.wireOp",EDGE,"E72.1");var subQ16=sQuery(id+"F12.wireOp",EDGE,"E74.1");var subQ18=sQuery(id+"F12.wireOp",EDGE,"E74.8");Q0=qUnion([makeQuery(id+"F12.imprint","IMPRINT",FACE,{"disambiguationData":[TD([[makeQuery(id+"F12.imprint","IMPRINT",EDGE,{"derivedFrom":subQ7}),1.0]])]}),makeQuery(id+"F12.imprint","IMPRINT",FACE,{"disambiguationData":[TD([[makeQuery(id+"F12.imprint","IMPRINT",EDGE,{"derivedFrom":subQ14}),1.0]])]}),makeQuery(id+"F12.imprint","IMPRINT",FACE,{"disambiguationData":[TD([[makeQuery(id+"F12.imprint","IMPRINT",EDGE,{"derivedFrom":subQ16}),1.0]])]}),makeQuery(id+"F12.imprint","IMPRINT",FACE,{"disambiguationData":[TD([[makeQuery(id+"F12.imprint","IMPRINT",EDGE,{"derivedFrom":subQ18}),-1.0]])]})]);}
            var Q1;
            Q1=makeQuery(id+"F5.boolean.opBoolean","SPLIT",FACE,{"disambiguationData":[TD([makeQuery(id+"F5.opExtrude","SWEPT_FACE",FACE,{"disambiguationData":[OSD([sQuery(id+"F4.wireOp",EDGE,"E41")])]})])],"derivedFrom":makeQuery(id+"F3.boolean.opBoolean","COPY",FACE,{"derivedFrom":makeQuery(id+"F3.opExtrude","CAP_FACE",FACE,{"disambiguationData":[OSD([sQuery(id+"F0.wireOp",EDGE,"E25.0"),sQuery(id+"F0.wireOp",EDGE,"E25.1"),sQuery(id+"F0.wireOp",EDGE,"E25.2"),sQuery(id+"F0.wireOp",EDGE,"E25.3"),sQuery(id+"F0.wireOp",EDGE,"E25.4"),sQuery(id+"F0.wireOp",EDGE,"E25.5"),sQuery(id+"F0.wireOp",EDGE,"E25.6"),sQuery(id+"F0.wireOp",EDGE,"E25.7")])],"isStart":false})})});
            extrude(context, id + "F13", {"entities" : qUnion([Q0]), "operationType" : NewBodyOperationType.REMOVE, "endBound" : BoundingType.UP_TO_SURFACE, "endBoundEntityFace" : qUnion([Q1]), "depth" : 25 * mm});
        }
        {
            var Q0;
            Q0=makeQuery(id+"F3.boolean.opBoolean","COPY",EDGE,{"derivedFrom":makeQuery(id+"F3.opExtrude","CAP_EDGE",EDGE,{"disambiguationData":[OSD([sQuery(id+"F0.wireOp",EDGE,"E25.6")])],"isStart":false})});
            var Q1;
            Q1=makeQuery(id+"F8.boolean.opBoolean","INTERSECT",EDGE,{"derivedFrom":[makeQuery(id+"F5.opExtrude","SWEPT_FACE",FACE,{"disambiguationData":[OSD([sQuery(id+"F4.wireOp",EDGE,"E30")])]}),makeQuery(id+"F8.opExtrude","CAP_FACE",FACE,{"disambiguationData":[OSD([sQuery(id+"F7.wireOp",EDGE,"E67")])],"isStart":false})]});
            var Q2;
            Q2=makeQuery(id+"F8.boolean.opBoolean","INTERSECT",EDGE,{"disambiguationData":[OD(1.0)],"derivedFrom":[makeQuery(id+"F5.opExtrude","SWEPT_FACE",FACE,{"disambiguationData":[OSD([sQuery(id+"F4.wireOp",EDGE,"E30")])]}),makeQuery(id+"F8.opExtrude","SWEPT_FACE",FACE,{"disambiguationData":[OSD([sQuery(id+"F7.wireOp",EDGE,"E67")])]})]});
            var Q3;
            {var subQ0=sQuery(id+"F4.wireOp",EDGE,"E30");Q3=makeQuery(id+"F8.boolean.opBoolean","SPLIT",EDGE,{"disambiguationData":[TD([makeQuery(id+"F5.opExtrude","SWEPT_FACE",FACE,{"disambiguationData":[OSD([sQuery(id+"F4.wireOp",EDGE,"E35.filletArc")])]})])],"derivedFrom":makeQuery(id+"F5.opExtrude","CAP_EDGE",EDGE,{"disambiguationData":[OSD([subQ0])],"isStart":false})});}
            var Q4;
            {var subQ0=sQuery(id+"F0.wireOp",EDGE,"E25.7");var subQ1=sQuery(id+"F0.wireOp",EDGE,"E25.1");var subQ2=sQuery(id+"F0.wireOp",EDGE,"E25.6");var subQ3=sQuery(id+"F0.wireOp",EDGE,"E25.5");var subQ4=sQuery(id+"F0.wireOp",EDGE,"E25.4");var subQ5=sQuery(id+"F0.wireOp",EDGE,"E25.0");var subQ6=sQuery(id+"F0.wireOp",EDGE,"E25.2");var subQ7=sQuery(id+"F0.wireOp",EDGE,"E25.3");Q4=makeQuery(id+"F8.boolean.opBoolean","INTERSECT",EDGE,{"derivedFrom":[makeQuery(id+"F5.boolean.opBoolean","SPLIT",FACE,{"disambiguationData":[TD([makeQuery(id+"F2.opExtrude","SWEPT_FACE",FACE,{"disambiguationData":[OSD([subQ5])]})])],"derivedFrom":makeQuery(id+"F3.boolean.opBoolean","COPY",FACE,{"derivedFrom":makeQuery(id+"F3.opExtrude","CAP_FACE",FACE,{"disambiguationData":[OSD([subQ5,subQ1,subQ6,subQ7,subQ4,subQ3,subQ2,subQ0])],"isStart":false})})}),makeQuery(id+"F8.opExtrude","SWEPT_FACE",FACE,{"disambiguationData":[OSD([sQuery(id+"F7.wireOp",EDGE,"E67")])]})]});}
            var Q5;
            Q5=makeQuery(id+"F8.boolean.opBoolean","INTERSECT",EDGE,{"disambiguationData":[OD(0.0)],"derivedFrom":[makeQuery(id+"F5.opExtrude","SWEPT_FACE",FACE,{"disambiguationData":[OSD([sQuery(id+"F4.wireOp",EDGE,"E30")])]}),makeQuery(id+"F8.opExtrude","SWEPT_FACE",FACE,{"disambiguationData":[OSD([sQuery(id+"F7.wireOp",EDGE,"E67")])]})]});
            fillet(context, id + "F14", {"entities" : qUnion([Q0, Q1, Q2, Q3, Q4, Q5]), "radius" : 3 * mm, "tangentPropagation" : true, "allowEdgeOverflow" : false});
        }
        {
            var Q0;
            Q0=makeQuery(id+"F1.opExtrude","CAP_EDGE",EDGE,{"disambiguationData":[OSD([sQuery(id+"F0.wireOp",EDGE,"E1.bottom")])],"isStart":false});
            fillet(context, id + "F15", {"entities" : qUnion([Q0]), "radius" : 2 * mm, "tangentPropagation" : true, "allowEdgeOverflow" : false});
        }
        {
            var Q0;
            {var subQ0=sQuery(id+"F0.wireOp",EDGE,"E21.filletArc");var subQ1=sQuery(id+"F0.wireOp",EDGE,"E7");var subQ2=sQuery(id+"F0.wireOp",EDGE,"E6");var subQ3=sQuery(id+"F0.wireOp",EDGE,"E5");var subQ4=sQuery(id+"F0.wireOp",EDGE,"E4");var subQ5=sQuery(id+"F0.wireOp",EDGE,"E22.filletArc");var subQ6=sQuery(id+"F0.wireOp",EDGE,"E1.bottom");var subQ7=sQuery(id+"F0.wireOp",EDGE,"E1.right");var subQ8=sQuery(id+"F0.wireOp",EDGE,"E1.top");var subQ9=sQuery(id+"F0.wireOp",EDGE,"E1.left");var subQ10=sQuery(id+"F0.wireOp",EDGE,"E23.filletArc");var subQ11=sQuery(id+"F0.wireOp",EDGE,"E24.filletArc");Q0=makeQuery(id+"F2.boolean.opBoolean","SPLIT",FACE,{"disambiguationData":[TD([makeQuery(id+"F1.opExtrude","SWEPT_FACE",FACE,{"disambiguationData":[OSD([subQ6])]})])],"derivedFrom":makeQuery(id+"F1.opExtrude","CAP_FACE",FACE,{"disambiguationData":[OSD([subQ6,subQ8,subQ9,subQ7,subQ4,subQ3,subQ2,subQ1,subQ0,subQ5,subQ10,subQ11])],"isStart":true})});}
            var sketch = newSketch(context, id + "F16", { "sketchPlane" : qUnion([Q0])});
            skLineSegment(sketch, "E79.0", {"start": v(-70, 90) * mm, "end": v(70, 90) * mm});
            skArc(sketch, "E79.1", {"start": v(-70, 90) * mm, "mid": v(-77.07, 87.07) * mm, "end": v(-80, 80) * mm});
            skLineSegment(sketch, "E79.2", {"start": v(-80, -80) * mm, "end": v(-80, 80) * mm});
            skArc(sketch, "E79.3", {"start": v(-80, -80) * mm, "mid": v(-77.07, -87.07) * mm, "end": v(-70, -90) * mm});
            skLineSegment(sketch, "E79.4", {"start": v(-70, -90) * mm, "end": v(70, -90) * mm});
            skArc(sketch, "E79.5", {"start": v(70, -90) * mm, "mid": v(77.07, -87.07) * mm, "end": v(80, -80) * mm});
            skLineSegment(sketch, "E79.6", {"start": v(80, -80) * mm, "end": v(80, 80) * mm});
            skArc(sketch, "E79.7", {"start": v(80, 80) * mm, "mid": v(77.07, 87.07) * mm, "end": v(70, 90) * mm});
            skArc(sketch, "E79.8", {"start": v(56.15, 48.18) * mm, "mid": v(0, 67.5) * mm, "end": v(-56.15, 48.18) * mm});
            skLineSegment(sketch, "E79.9", {"start": v(60, 40.3) * mm, "end": v(60, -40.3) * mm});
            skArc(sketch, "E79.10", {"start": v(60, 40.3) * mm, "mid": v(58.99, 44.68) * mm, "end": v(56.15, 48.18) * mm});
            skArc(sketch, "E79.11", {"start": v(-56.15, 48.18) * mm, "mid": v(-58.99, 44.68) * mm, "end": v(-60, 40.3) * mm});
            skLineSegment(sketch, "E79.12", {"start": v(-60, 40.3) * mm, "end": v(-60, -40.3) * mm});
            skArc(sketch, "E79.13", {"start": v(-60, -40.3) * mm, "mid": v(-58.99, -44.68) * mm, "end": v(-56.15, -48.18) * mm});
            skArc(sketch, "E79.14", {"start": v(-56.15, -48.18) * mm, "mid": v(0, -67.5) * mm, "end": v(56.15, -48.18) * mm});
            skArc(sketch, "E79.15", {"start": v(56.15, -48.18) * mm, "mid": v(58.99, -44.68) * mm, "end": v(60, -40.3) * mm});
            skCircle(sketch, "E79.16", {"center": v(60, -67.5) * mm, "radius": 4 * mm});
            skCircle(sketch, "E79.17", {"center": v(60, 67.5) * mm, "radius": 4 * mm});
            skCircle(sketch, "E79.18", {"center": v(-60, 67.5) * mm, "radius": 4 * mm});
            skCircle(sketch, "E79.19", {"center": v(-60, -67.5) * mm, "radius": 4 * mm});
            skPoint(sketch, "E79.20", {"position": v(58.99, 44.68) * mm});
            skPoint(sketch, "E79.21", {"position": v(58.99, -44.68) * mm});
            skLineSegment(sketch, "E80", {"start": v(0, 90) * mm, "end": v(0, 120) * mm, "construction": true});
            skPoint(sketch, "E80.endSnap0", {"position": v(0, 90) * mm});
            skCircle(sketch, "E81", {"center": v(0, 120) * mm, "radius": 6 * mm});
            skArc(sketch, "E82", {"start": v(15, 120) * mm, "mid": v(0, 135) * mm, "end": v(-15, 120) * mm});
            skLineSegment(sketch, "E83", {"start": v(-15, 120) * mm, "end": v(-15, 108) * mm});
            skLineSegment(sketch, "E84", {"start": v(15, 120) * mm, "end": v(15, 108) * mm});
            skLineSegment(sketch, "E85", {"start": v(-15, 108) * mm, "end": v(-33, 90) * mm});
            skLineSegment(sketch, "E86", {"start": v(15, 108) * mm, "end": v(33, 90) * mm});
            skLineSegment(sketch, "E87", {"start": v(-80, 0) * mm, "end": v(80, 0) * mm, "construction": true});
            skArc(sketch, "E88.MirrorCS", {"start": v(-15, 120) * mm, "mid": v(0, 135) * mm, "end": v(15, 120) * mm});
            skLineSegment(sketch, "E89.MirrorCS", {"start": v(80, 0) * mm, "end": v(-80, 0) * mm, "construction": true});
            skArc(sketch, "E90.MirrorCS", {"start": v(-15, -120) * mm, "mid": v(0, -135) * mm, "end": v(15, -120) * mm});
            skCircle(sketch, "E91.MirrorC", {"center": v(0, -120) * mm, "radius": 6 * mm});
            skLineSegment(sketch, "E92.MirrorCS", {"start": v(15, -108) * mm, "end": v(33, -90) * mm});
            skLineSegment(sketch, "E93.MirrorCS", {"start": v(-15, -120) * mm, "end": v(-15, -108) * mm});
            skLineSegment(sketch, "E94.MirrorCS", {"start": v(15, -120) * mm, "end": v(15, -108) * mm});
            skLineSegment(sketch, "E95.MirrorCS", {"start": v(-15, -108) * mm, "end": v(-33, -90) * mm});
            skPoint(sketch, "E96.MirrorP", {"position": v(0, -90) * mm});
            skArc(sketch, "E97.MirrorCS", {"start": v(15, -120) * mm, "mid": v(0, -135) * mm, "end": v(-15, -120) * mm});
            skLineSegment(sketch, "E98.MirrorCS", {"start": v(0, -90) * mm, "end": v(0, -120) * mm, "construction": true});
            skSolve(sketch);
        }
        {
            var Q0;
            {var subQ1=sQuery(id+"F16.wireOp",EDGE,"E79.1");Q0=makeQuery(id+"F16.imprint","IMPRINT",FACE,{"disambiguationData":[TD([[makeQuery(id+"F16.imprint","IMPRINT",EDGE,{"derivedFrom":subQ1}),1.0]])]});}
            var Q1;
            {var subQ0=sQuery(id+"F16.wireOp",EDGE,"E86");Q1=makeQuery(id+"F16.imprint","IMPRINT",FACE,{"disambiguationData":[TD([[makeQuery(id+"F16.imprint","IMPRINT",EDGE,{"derivedFrom":subQ0}),-1.0]])]});}
            var Q2;
            Q2=makeQuery(id+"F16.imprint","IMPRINT",FACE,{"disambiguationData":[TD([[makeQuery(id+"F16.imprint","IMPRINT",EDGE,{"derivedFrom":sQuery(id+"F16.wireOp",EDGE,"E90.MirrorCS")}),1.0]])]});
            var Q3;
            Q3=makeQuery(id+"F2.opExtrude","CAP_FACE",FACE,{"disambiguationData":[OSD([sQuery(id+"F0.wireOp",EDGE,"E12"),sQuery(id+"F0.wireOp",EDGE,"E13"),sQuery(id+"F0.wireOp",EDGE,"E14"),sQuery(id+"F0.wireOp",EDGE,"E15"),sQuery(id+"F0.wireOp",EDGE,"E17.filletArc"),sQuery(id+"F0.wireOp",EDGE,"E18.filletArc"),sQuery(id+"F0.wireOp",EDGE,"E19.filletArc"),sQuery(id+"F0.wireOp",EDGE,"E20.filletArc"),sQuery(id+"F0.wireOp",EDGE,"E25.0"),sQuery(id+"F0.wireOp",EDGE,"E25.1"),sQuery(id+"F0.wireOp",EDGE,"E25.2"),sQuery(id+"F0.wireOp",EDGE,"E25.3"),sQuery(id+"F0.wireOp",EDGE,"E25.4"),sQuery(id+"F0.wireOp",EDGE,"E25.5"),sQuery(id+"F0.wireOp",EDGE,"E25.6"),sQuery(id+"F0.wireOp",EDGE,"E25.7")])],"isStart":false});
            extrude(context, id + "F17", {"entities" : qUnion([Q0, Q1, Q2]), "endBound" : BoundingType.UP_TO_SURFACE, "endBoundEntityFace" : qUnion([Q3]), "depth" : 25 * mm});
        }
    });
